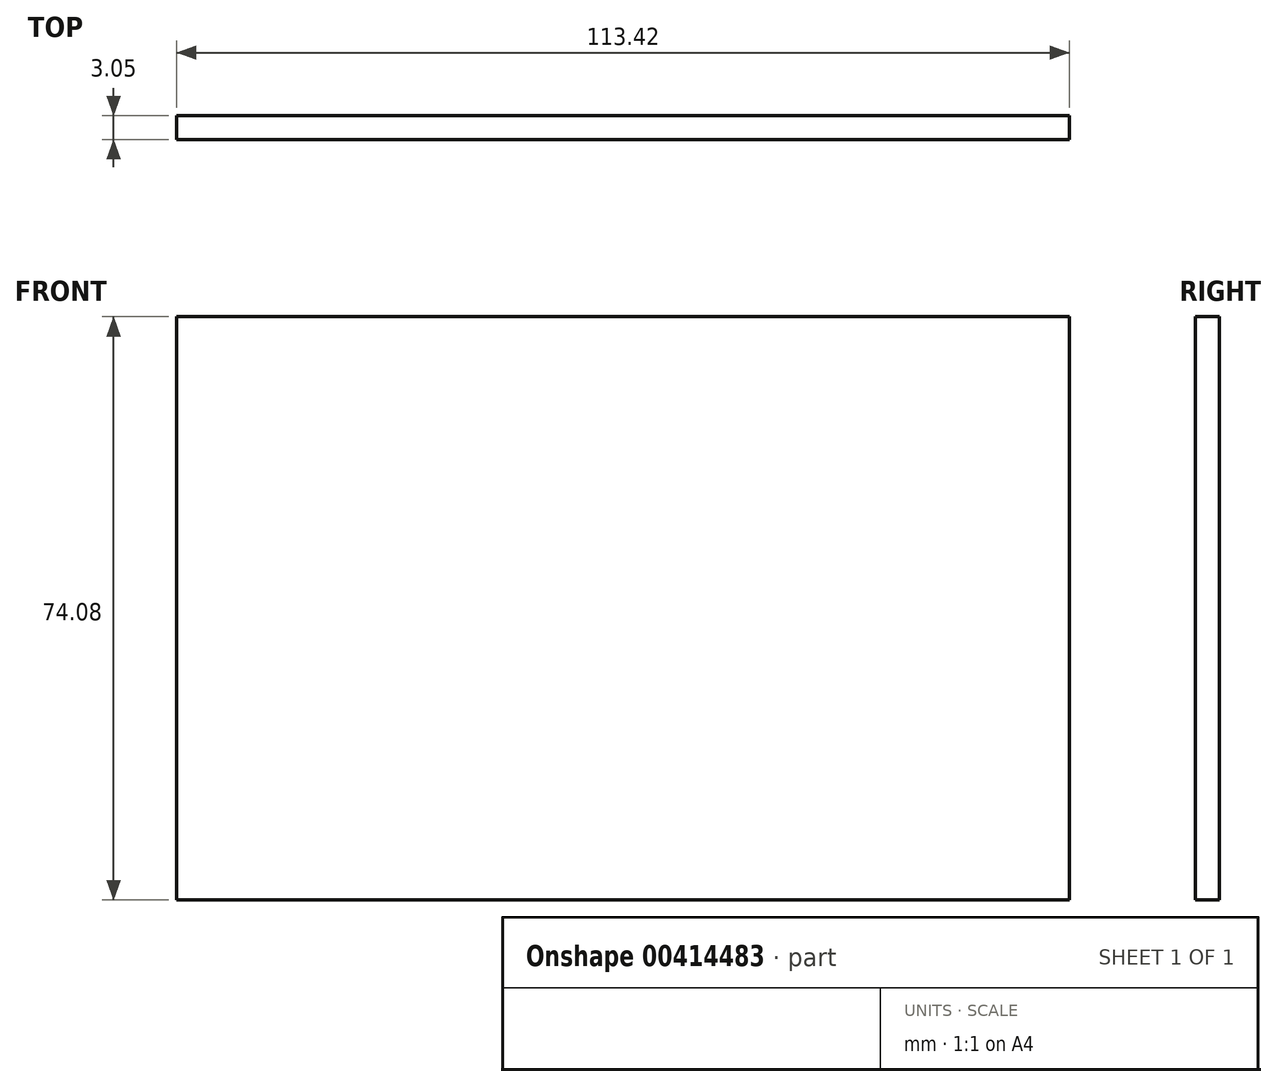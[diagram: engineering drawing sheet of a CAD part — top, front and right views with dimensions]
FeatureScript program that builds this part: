
annotation { "Feature Type Name" : "Feature", "Feature Type Description" : "" }
export const myFeature = defineFeature(function(context is Context, id is Id, definition is map)
    precondition{}
    {
        {
            var Q0;
            Q0=qCreatedBy(makeId("Front.planeOp"),FACE);
            var sketch = newSketch(context, id + "F0", { "sketchPlane" : qUnion([Q0])});
            skLineSegment(sketch, "E0.bottom", {"start": v(-56.7, 37.04) * mm, "end": v(56.7, 37.04) * mm});
            skLineSegment(sketch, "E0.top", {"start": v(-56.7, -37.04) * mm, "end": v(56.7, -37.04) * mm});
            skLineSegment(sketch, "E0.left", {"start": v(-56.7, 37.04) * mm, "end": v(-56.7, -37.04) * mm});
            skLineSegment(sketch, "E0.right", {"start": v(56.7, 37.04) * mm, "end": v(56.7, -37.04) * mm});
            skPoint(sketch, "E0.middle", {"position": v(0, 0) * mm});
            skSolve(sketch);
        }
        {
            var Q0;
            Q0=makeQuery(id+"F0.imprint","IMPRINT",FACE,{"disambiguationData":[TD([[makeQuery(id+"F0.imprint","IMPRINT",EDGE,{"derivedFrom":sQuery(id+"F0.wireOp",EDGE,"E0.bottom")}),-1.0]])]});
            extrude(context, id + "F1", {"entities" : qUnion([Q0]), "depth" : 3.05 * mm});
        }
        {
            var Q0;
            Q0=makeQuery(id+"F1.opExtrude","CAP_FACE",FACE,{"disambiguationData":[OSD([sQuery(id+"F0.wireOp",EDGE,"E0.bottom"),sQuery(id+"F0.wireOp",EDGE,"E0.top"),sQuery(id+"F0.wireOp",EDGE,"E0.left"),sQuery(id+"F0.wireOp",EDGE,"E0.right")])],"isStart":false});
            var sketch = newSketch(context, id + "F2", { "sketchPlane" : qUnion([Q0])});
            skCircle(sketch, "E1", {"center": v(0, 0) * mm, "radius": 29.56 * mm});
            skSolve(sketch);
        }
        {
            var Q0;
            Q0=makeQuery(id+"F2.imprint","IMPRINT",FACE,{"disambiguationData":[TD([[makeQuery(id+"F2.imprint","IMPRINT",EDGE,{"derivedFrom":sQuery(id+"F2.wireOp",EDGE,"E1")}),1.0]])]});
            var sketch = newSketch(context, id + "F3", { "sketchPlane" : qUnion([Q0])});
            skCircle(sketch, "E2", {"center": v(0, 0) * mm, "radius": 25.81 * mm});
            skSolve(sketch);
        }
        {
            var Q0;
            Q0=sQuery(id+"F3.wireOp",EDGE,"E2");
            var Q1;
            Q1=sQuery(id+"F2.wireOp",EDGE,"E1");
            extrude(context, id + "F4", {"bodyType" : ToolBodyType.SURFACE, "surfaceEntities" : qUnion([Q0, Q1]), "depth" : 25.4 * mm, "hasSecondDirection" : true, "secondDirectionOppositeDirection" : true, "secondDirectionDepth" : 3.17 * mm});
        }
    });
